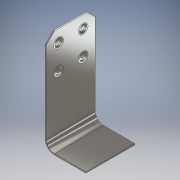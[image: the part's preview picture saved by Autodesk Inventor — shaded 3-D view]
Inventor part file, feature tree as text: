
AUTODESK INVENTOR PART (.ipt)
format: ipt  version: 2018 (Build 220112000, 112)  size: 151,552 bytes
history: native  units: mm
features: sketch x2, extrude x1, hole x1, fillet x1, chamfer x1, projected_geometry x1
ambient origin geometry x8: Origin, YZ Plane, XZ Plane, XY Plane, X Axis, Y Axis, Z Axis, Center Point
bodies: Solid1 (feature_tree)
feature tree (7):
  extrude  "Extrusion1"  Depth=6.0mm TaperAngle=0.0deg
  hole  "Hole1"  [1 undecoded]
  fillet  "Fillet1"  Radius=1.0mm
  chamfer  "Chamfer1"  Distance=1.0mm Angle=45.0deg
  sketch  "Sketch1"  dims[d0=0.15mm d1=12.15mm d2=1.0mm d3=5.0mm d4=6.0mm d5=0.0mm]
  sketch  "Sketch2"  dims[d6=9.15mm d7=3.0mm d8=0.6mm d9=6.0mm d10=4.0mm d11=2.0mm d12=90.0deg d13=0.05mm d14=0.0mm d15=1.0mm d16=1.0mm d17=2.0mm d18=45.0deg]
  projected_geometry  "Projected Loop1"
note: 1 required parameter value undecoded (feature->parameter linkage not recoverable at this tier; creation-order binding heuristic only, values carry confidence <= 0.55)
